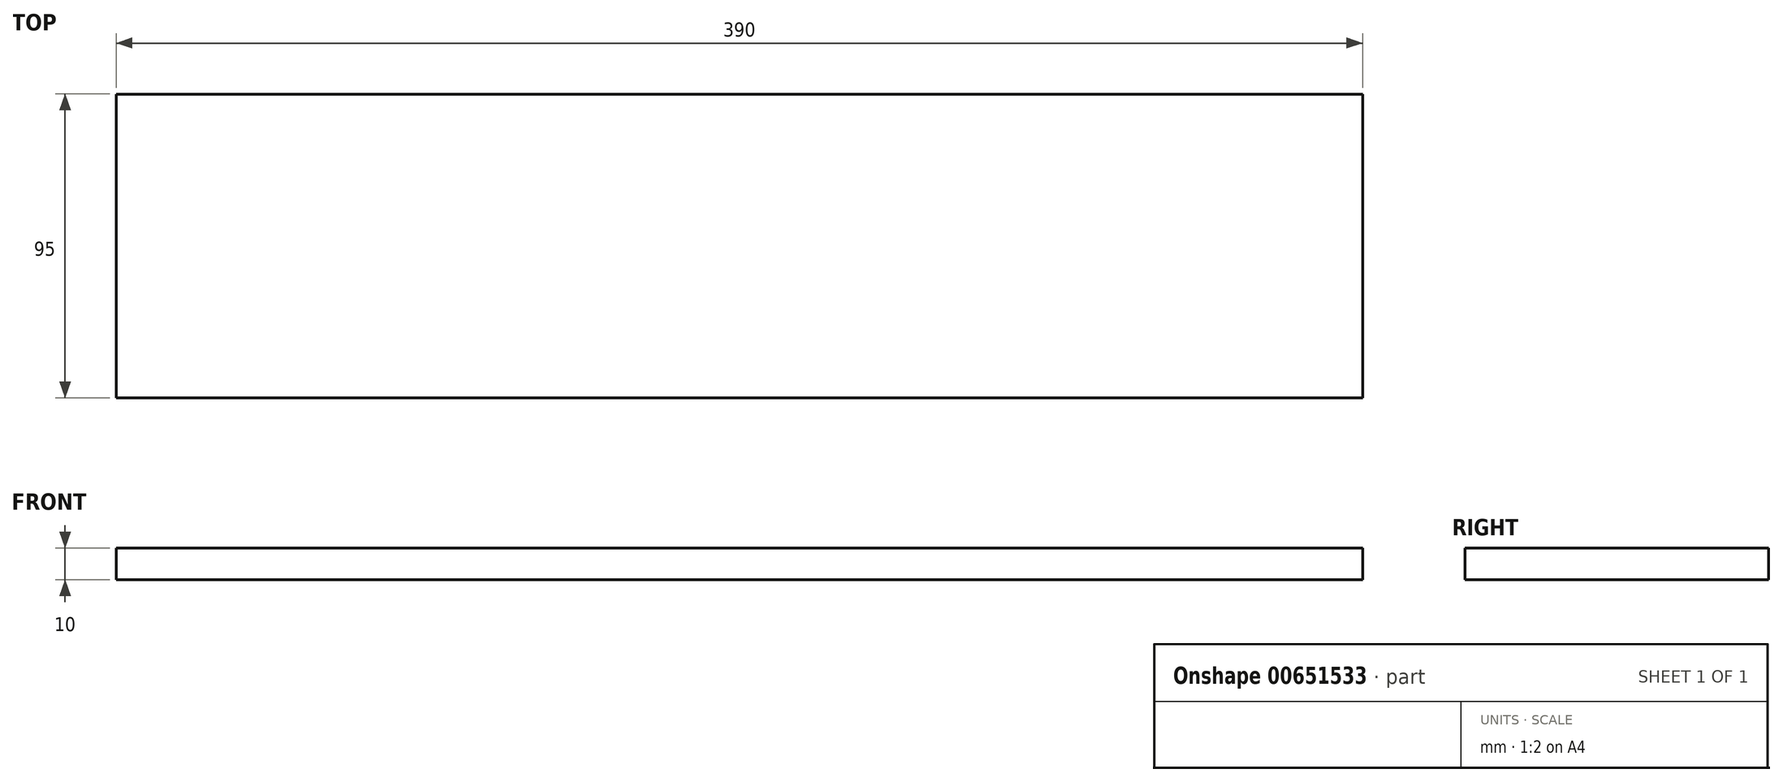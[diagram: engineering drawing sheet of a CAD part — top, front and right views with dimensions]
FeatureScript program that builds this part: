
annotation { "Feature Type Name" : "Feature", "Feature Type Description" : "" }
export const myFeature = defineFeature(function(context is Context, id is Id, definition is map)
    precondition{}
    {
        {
            assignVariable(context, id + "F0", {"name" : "d", "anyValue" : 10});
        }
        {
            var Q0;
            Q0=qCreatedBy(makeId("Top.planeOp"),FACE);
            var sketch = newSketch(context, id + "F1", { "sketchPlane" : qUnion([Q0])});
            skLineSegment(sketch, "E0.bottom", {"start": v(-190, -53.22) * mm, "end": v(200, -53.22) * mm});
            skLineSegment(sketch, "E0.top", {"start": v(-190, 41.78) * mm, "end": v(200, 41.78) * mm});
            skLineSegment(sketch, "E0.left", {"start": v(-190, -53.22) * mm, "end": v(-190, 41.78) * mm});
            skLineSegment(sketch, "E0.right", {"start": v(200, -53.22) * mm, "end": v(200, 41.78) * mm});
            skSolve(sketch);
        }
        {
            var Q0;
            Q0=makeQuery(id+"F1.imprint","IMPRINT",FACE,{"disambiguationData":[TD([[makeQuery(id+"F1.imprint","IMPRINT",EDGE,{"derivedFrom":sQuery(id+"F1.wireOp",EDGE,"E0.bottom")}),1.0]])]});
            extrude(context, id + "F2", {"entities" : qUnion([Q0]), "depth" : (getVariable(context, 'd')) * mm, "offsetDistance" : 25 * mm});
        }
    });
